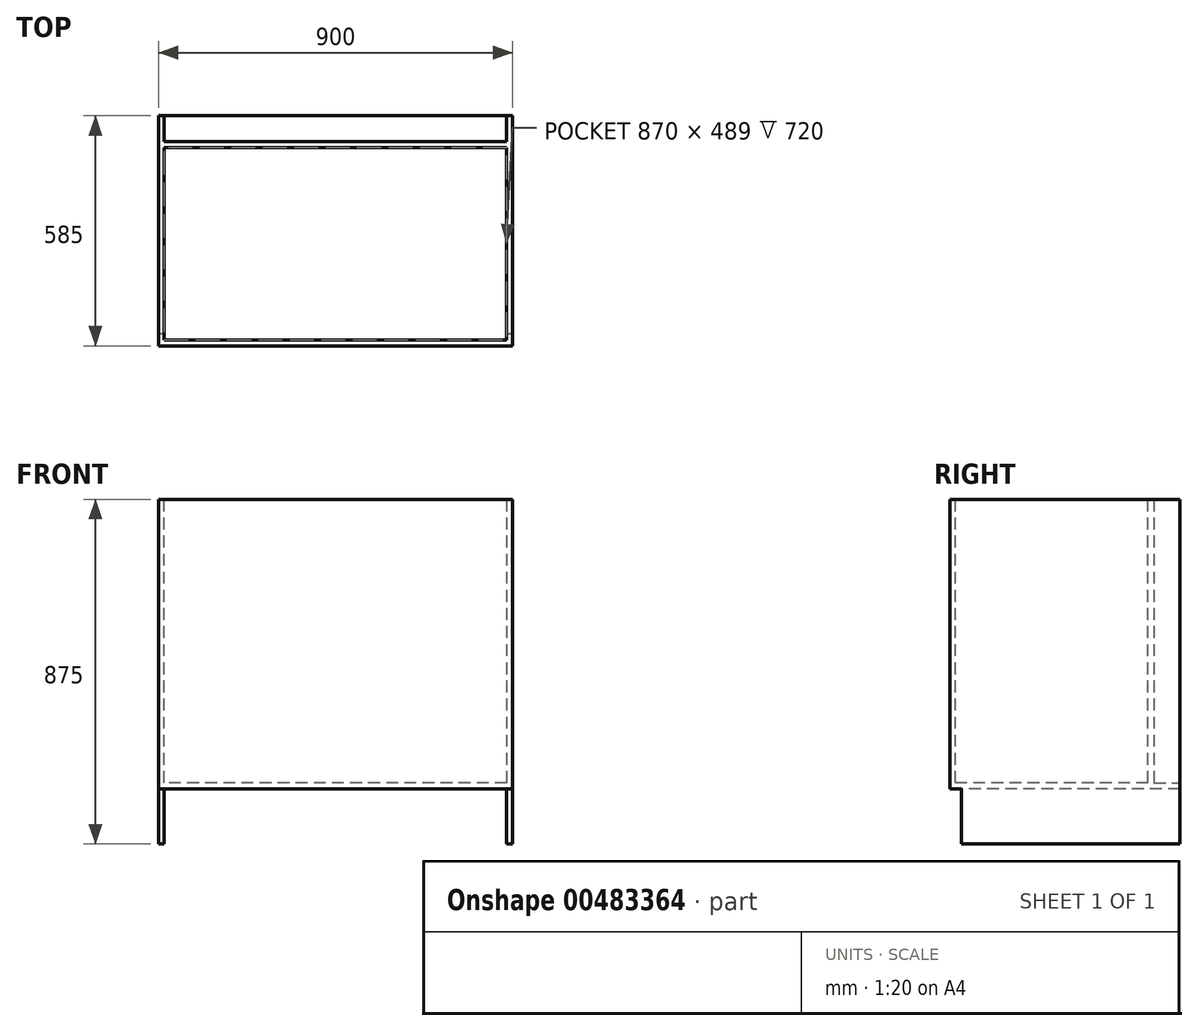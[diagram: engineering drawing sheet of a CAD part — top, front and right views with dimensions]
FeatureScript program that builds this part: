
annotation { "Feature Type Name" : "Feature", "Feature Type Description" : "" }
export const myFeature = defineFeature(function(context is Context, id is Id, definition is map)
    precondition{}
    {
        {
            var Q0;
            Q0=qCreatedBy(makeId("Right.planeOp"),FACE);
            var sketch = newSketch(context, id + "F0", { "sketchPlane" : qUnion([Q0])});
            skLineSegment(sketch, "E0", {"start": v(0, 0) * mm, "end": v(0, 735) * mm});
            skLineSegment(sketch, "E1", {"start": v(0, 735) * mm, "end": v(570, 735) * mm});
            skLineSegment(sketch, "E2", {"start": v(570, 735) * mm, "end": v(570, 0) * mm});
            skLineSegment(sketch, "E3", {"start": v(570, 0) * mm, "end": v(570, -140) * mm});
            skLineSegment(sketch, "E4", {"start": v(570, -140) * mm, "end": v(15, -140) * mm});
            skLineSegment(sketch, "E5", {"start": v(15, -140) * mm, "end": v(15, 0) * mm});
            skLineSegment(sketch, "E6", {"start": v(15, 0) * mm, "end": v(0, 0) * mm});
            skSolve(sketch);
        }
        {
            var Q0;
            Q0=qCreatedBy(makeId("Top.planeOp"),FACE);
            var sketch = newSketch(context, id + "F1", { "sketchPlane" : qUnion([Q0])});
            skLineSegment(sketch, "E7", {"start": v(0, 0) * mm, "end": v(885, 0) * mm});
            skLineSegment(sketch, "E8", {"start": v(885, 0) * mm, "end": v(885, 570) * mm});
            skLineSegment(sketch, "E9", {"start": v(885, 570) * mm, "end": v(0, 570) * mm});
            skLineSegment(sketch, "E10", {"start": v(0, 570) * mm, "end": v(0, 0) * mm});
            skSolve(sketch);
        }
        {
            var Q0;
            Q0=makeQuery(id+"F0.imprint","IMPRINT",FACE,{"disambiguationData":[TD([[makeQuery(id+"F0.imprint","IMPRINT",EDGE,{"derivedFrom":sQuery(id+"F0.wireOp",EDGE,"E0")}),-1.0]])]});
            extrude(context, id + "F2", {"entities" : qUnion([Q0]), "depth" : 15 * mm});
        }
        {
            var Q0;
            Q0=qSketchRegion(id+"F1",true);
            extrude(context, id + "F3", {"entities" : qUnion([Q0]), "operationType" : NewBodyOperationType.ADD, "depth" : 15 * mm});
        }
        {
            var Q0;
            Q0=qCreatedBy(makeId("Front.planeOp"),FACE);
            var sketch = newSketch(context, id + "F4", { "sketchPlane" : qUnion([Q0])});
            skLineSegment(sketch, "E11", {"start": v(0, 0) * mm, "end": v(0, 735) * mm});
            skLineSegment(sketch, "E12", {"start": v(0, 735) * mm, "end": v(900, 735) * mm});
            skLineSegment(sketch, "E13", {"start": v(900, 735) * mm, "end": v(900, 0) * mm});
            skLineSegment(sketch, "E14", {"start": v(900, 0) * mm, "end": v(0, 0) * mm});
            skSolve(sketch);
        }
        {
            var Q0;
            Q0=makeQuery(id+"F4.imprint","IMPRINT",FACE,{"disambiguationData":[TD([[makeQuery(id+"F4.imprint","IMPRINT",EDGE,{"derivedFrom":sQuery(id+"F4.wireOp",EDGE,"E11")}),-1.0]])]});
            extrude(context, id + "F5", {"entities" : qUnion([Q0]), "operationType" : NewBodyOperationType.ADD, "depth" : 15 * mm});
        }
        {
            var Q0;
            Q0=makeQuery(id+"F3.opExtrude","SWEPT_FACE",FACE,{"disambiguationData":[OSD([sQuery(id+"F1.wireOp",EDGE,"E8")])]});
            cPlane(context, id + "F6", {"entities" : qUnion([Q0]), "cplaneType" : CPlaneType.OFFSET, "offset" : 0 * mm, "width" : 150 * mm, "height" : 150 * mm});
        }
        {
            var Q0;
            Q0=qCreatedBy(id+"F6.planeOp",FACE);
            var sketch = newSketch(context, id + "F7", { "sketchPlane" : qUnion([Q0])});
            skLineSegment(sketch, "E15", {"start": v(0, 0) * mm, "end": v(15, 0) * mm});
            skLineSegment(sketch, "E16", {"start": v(15, 0) * mm, "end": v(15, -140) * mm});
            skLineSegment(sketch, "E17", {"start": v(15, -140) * mm, "end": v(570, -140) * mm});
            skLineSegment(sketch, "E18", {"start": v(570, -140) * mm, "end": v(570, 735) * mm});
            skLineSegment(sketch, "E19", {"start": v(570, 735) * mm, "end": v(0, 735) * mm});
            skLineSegment(sketch, "E20", {"start": v(0, 735) * mm, "end": v(0, 0) * mm});
            skSolve(sketch);
        }
        {
            var Q0;
            Q0=qSketchRegion(id+"F7",true);
            extrude(context, id + "F8", {"entities" : qUnion([Q0]), "operationType" : NewBodyOperationType.ADD, "depth" : 15 * mm});
        }
        {
            var Q0;
            Q0=makeQuery(id+"F8.boolean.opBoolean","MERGE",FACE,{"derivedFrom":[makeQuery(id+"F3.boolean.opBoolean","MERGE",FACE,{"derivedFrom":[makeQuery(id+"F2.opExtrude","SWEPT_FACE",FACE,{"disambiguationData":[OSD([sQuery(id+"F0.wireOp",EDGE,"E2"),sQuery(id+"F0.wireOp",EDGE,"E3")])]}),makeQuery(id+"F3.opExtrude","SWEPT_FACE",FACE,{"disambiguationData":[OSD([sQuery(id+"F1.wireOp",EDGE,"E9")])]})]}),makeQuery(id+"F8.opExtrude","SWEPT_FACE",FACE,{"disambiguationData":[OSD([sQuery(id+"F7.wireOp",EDGE,"E18")])]})]});
            cPlane(context, id + "F9", {"entities" : qUnion([Q0]), "cplaneType" : CPlaneType.OFFSET, "offset" : 66 * mm, "oppositeDirection" : true, "width" : 150 * mm, "height" : 150 * mm});
        }
        {
            var Q0;
            Q0=qCreatedBy(id+"F9.planeOp",FACE);
            var sketch = newSketch(context, id + "F10", { "sketchPlane" : qUnion([Q0])});
            skLineSegment(sketch, "E21", {"start": v(0, 0) * mm, "end": v(0, 15) * mm});
            skLineSegment(sketch, "E22", {"start": v(0, 15) * mm, "end": v(-15, 15) * mm});
            skLineSegment(sketch, "E23", {"start": v(-15, 15) * mm, "end": v(-15, 735) * mm});
            skLineSegment(sketch, "E24", {"start": v(-15, 735) * mm, "end": v(-885, 735) * mm});
            skLineSegment(sketch, "E25", {"start": v(-885, 735) * mm, "end": v(-885, 15) * mm});
            skLineSegment(sketch, "E26", {"start": v(-885, 15) * mm, "end": v(-15, 15) * mm});
            skSolve(sketch);
        }
        {
            var Q0;
            Q0=makeQuery(id+"F10.imprint","IMPRINT",FACE,{"disambiguationData":[TD([[makeQuery(id+"F10.imprint","IMPRINT",EDGE,{"derivedFrom":sQuery(id+"F10.wireOp",EDGE,"E23")}),1.0]])]});
            extrude(context, id + "F11", {"entities" : qUnion([Q0]), "operationType" : NewBodyOperationType.ADD, "oppositeDirection" : true, "depth" : 15 * mm});
        }
    });
